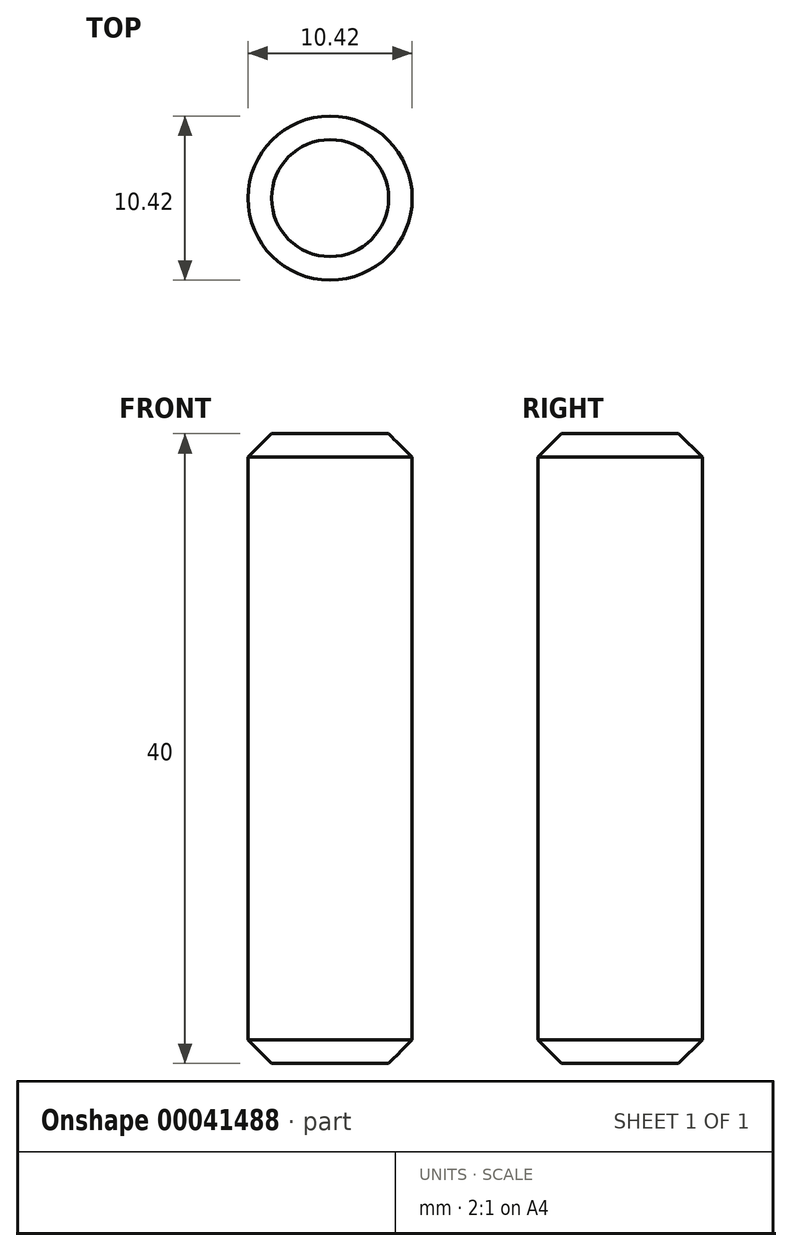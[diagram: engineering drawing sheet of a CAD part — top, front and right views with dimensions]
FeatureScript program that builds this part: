
annotation { "Feature Type Name" : "Feature", "Feature Type Description" : "" }
export const myFeature = defineFeature(function(context is Context, id is Id, definition is map)
    precondition{}
    {
        {
            var Q0;
            Q0=qCreatedBy(makeId("Top.planeOp"),FACE);
            var sketch = newSketch(context, id + "F0", { "sketchPlane" : qUnion([Q0])});
            skCircle(sketch, "E0", {"center": v(0, 0) * mm, "radius": 5.21 * mm});
            skSolve(sketch);
        }
        {
            var Q0;
            Q0 = qSketchRegion(id + "F0", true);
            var Q1;
            Q1 = qConstructionFilter(qBodyType(qCreatedBy(id + "F0" ,EDGE), BodyType.WIRE), ConstructionObject.NO);
            extrude(context, id + "F1", {"entities" : qUnion([Q0]), "surfaceEntities" : qUnion([Q1]), "depth" : 40 * mm});
        }
        {
            var Q0;
            Q0=makeQuery(id+"F1.opExtrude","CAP_EDGE",EDGE,{"disambiguationData":[OSD([sQuery(id+"F0.wireOp",EDGE,"E0")])],"isStart":true});
            var Q1;
            Q1=makeQuery(id+"F1.opExtrude","CAP_EDGE",EDGE,{"disambiguationData":[OSD([sQuery(id+"F0.wireOp",EDGE,"E0")])],"isStart":false});
            chamfer(context, id + "F2", {"entities" : qUnion([Q0, Q1]), "width" : 1.5 * mm, "tangentPropagation" : true});
        }
    });
